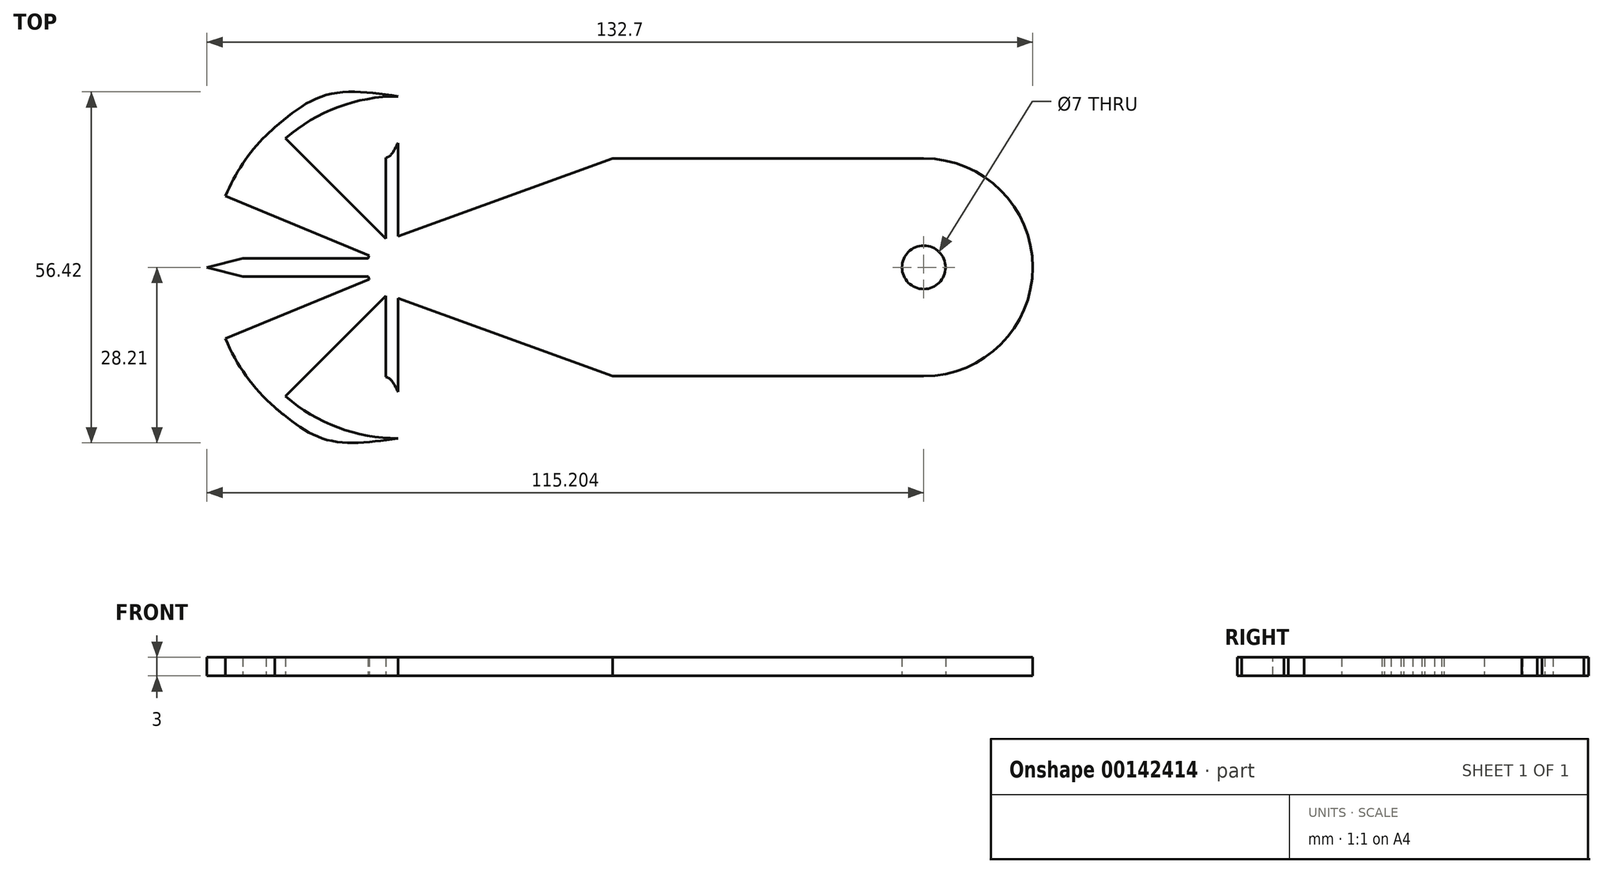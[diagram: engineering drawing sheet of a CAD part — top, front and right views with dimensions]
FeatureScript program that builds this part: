
annotation { "Feature Type Name" : "Feature", "Feature Type Description" : "" }
export const myFeature = defineFeature(function(context is Context, id is Id, definition is map)
    precondition{}
    {
        {
            var Q0;
            Q0=qCreatedBy(makeId("Top.planeOp"),FACE);
            var sketch = newSketch(context, id + "F0", { "sketchPlane" : qUnion([Q0])});
            skLineSegment(sketch, "E0", {"start": v(-142.5, 0) * mm, "end": v(-112.5, 0) * mm, "construction": true});
            skPoint(sketch, "E0.endSnap0", {"position": v(-142.5, 0) * mm});
            skArc(sketch, "E1", {"start": v(-117.12, 1.91) * mm, "mid": v(-117.2, 1.7) * mm, "end": v(-117.28, 1.46) * mm});
            skLineSegment(sketch, "E2", {"start": v(-112.5, 5) * mm, "end": v(-112.5, -5) * mm, "construction": true});
            skLineSegment(sketch, "E3", {"start": v(-112.5, 0) * mm, "end": v(-107.5, 0) * mm, "construction": true});
            skLineSegment(sketch, "E4", {"start": v(-112.5, 0) * mm, "end": v(-117.5, 0) * mm, "construction": true});
            skLineSegment(sketch, "E5", {"start": v(-117.5, 0) * mm, "end": v(-112.5, 5) * mm, "construction": true});
            skLineSegment(sketch, "E6", {"start": v(-112.5, 0) * mm, "end": v(-115, 2.5) * mm, "construction": true});
            skLineSegment(sketch, "E7", {"start": v(-112.5, 5) * mm, "end": v(-107.5, 0) * mm, "construction": true});
            skLineSegment(sketch, "E8", {"start": v(-107.5, 0) * mm, "end": v(-112.5, -5) * mm, "construction": true});
            skLineSegment(sketch, "E9", {"start": v(-112.5, -5) * mm, "end": v(-117.5, 0) * mm, "construction": true});
            skLineSegment(sketch, "E10", {"start": v(-115, 2.5) * mm, "end": v(-116.04, 3.54) * mm, "construction": true});
            skLineSegment(sketch, "E11", {"start": v(-112.5, 0) * mm, "end": v(-115, -2.5) * mm, "construction": true});
            skLineSegment(sketch, "E12", {"start": v(-115, -2.5) * mm, "end": v(-116.04, -3.54) * mm, "construction": true});
            skLineSegment(sketch, "E13", {"start": v(-116.04, 3.54) * mm, "end": v(-116.04, -3.54) * mm, "construction": true});
            skLineSegment(sketch, "E14", {"start": v(-116.04, 3.54) * mm, "end": v(-108.96, 3.54) * mm, "construction": true});
            skLineSegment(sketch, "E15", {"start": v(-108.96, 3.54) * mm, "end": v(-108.96, -3.54) * mm, "construction": true});
            skLineSegment(sketch, "E16", {"start": v(-108.96, -3.54) * mm, "end": v(-116.04, -3.54) * mm, "construction": true});
            skLineSegment(sketch, "E17", {"start": v(-116.04, 1.46) * mm, "end": v(-117.28, 1.46) * mm, "construction": true});
            skLineSegment(sketch, "E18", {"start": v(-116.04, -1.46) * mm, "end": v(-117.28, -1.46) * mm, "construction": true});
            skLineSegment(sketch, "E19", {"start": v(-117.28, 1.46) * mm, "end": v(-135.56, 1.46) * mm});
            skLineSegment(sketch, "E20", {"start": v(-117.28, -1.46) * mm, "end": v(-135.56, -1.46) * mm});
            skLineSegment(sketch, "E21", {"start": v(-112.5, 0) * mm, "end": v(-116.04, -1.46) * mm, "construction": true});
            skLineSegment(sketch, "E22", {"start": v(-116.04, -1.46) * mm, "end": v(-117.12, -1.91) * mm, "construction": true});
            skLineSegment(sketch, "E23", {"start": v(-112.5, 0) * mm, "end": v(-116.04, 1.46) * mm, "construction": true});
            skLineSegment(sketch, "E24", {"start": v(-116.04, 1.46) * mm, "end": v(-117.12, 1.91) * mm, "construction": true});
            skLineSegment(sketch, "E25", {"start": v(-112.5, 0) * mm, "end": v(-113.96, -3.54) * mm, "construction": true});
            skLineSegment(sketch, "E26", {"start": v(-113.96, -3.54) * mm, "end": v(-114.41, -4.62) * mm, "construction": true});
            skLineSegment(sketch, "E27", {"start": v(-112.5, 0) * mm, "end": v(-113.96, 3.54) * mm, "construction": true});
            skLineSegment(sketch, "E28", {"start": v(-113.96, 3.54) * mm, "end": v(-114.41, 4.62) * mm, "construction": true});
            skLineSegment(sketch, "E29", {"start": v(-114.41, -4.62) * mm, "end": v(-127.3, -17.5) * mm});
            skLineSegment(sketch, "E30", {"start": v(-127.3, -17.5) * mm, "end": v(-130.55, -20.75) * mm});
            skArc(sketch, "E31.trimOffspring", {"start": v(-133.71, -21.21) * mm, "mid": v(-133.03, -21.88) * mm, "end": v(-132.32, -22.52) * mm, "construction": true});
            skArc(sketch, "E32.trimOffspring", {"start": v(-133.71, -21.21) * mm, "mid": v(-133.03, -21.88) * mm, "end": v(-132.32, -22.52) * mm});
            skLineSegment(sketch, "E33", {"start": v(-142.5, 0) * mm, "end": v(-143.2, 0) * mm, "construction": true});
            skLineSegment(sketch, "E34", {"start": v(-137.46, 1.46) * mm, "end": v(-143.2, 0) * mm});
            skLineSegment(sketch, "E35", {"start": v(-143.2, 0) * mm, "end": v(-137.46, -1.46) * mm});
            skLineSegment(sketch, "E36.trimOffspring", {"start": v(-142.46, -1.46) * mm, "end": v(-142.5, -1.46) * mm});
            skLineSegment(sketch, "E37.trimOffspring", {"start": v(-142.46, 1.46) * mm, "end": v(-142.5, 1.46) * mm});
            skLineSegment(sketch, "E38", {"start": v(-112.5, 0) * mm, "end": v(-143.2, 0) * mm, "construction": true});
            skArc(sketch, "E39", {"start": v(-143.2, 0) * mm, "mid": v(-127.88, 26.57) * mm, "end": v(-97.2, 26.62) * mm, "construction": true});
            skArc(sketch, "E40", {"start": v(-143.2, 0) * mm, "mid": v(-130.41, -24.93) * mm, "end": v(-102.7, -29.1) * mm, "construction": true});
            skArc(sketch, "E41", {"start": v(-132.32, -22.52) * mm, "mid": v(-131.6, -23.14) * mm, "end": v(-130.86, -23.73) * mm});
            skLineSegment(sketch, "E42", {"start": v(-112.5, 0) * mm, "end": v(-112.5, -30) * mm, "construction": true});
            skLineSegment(sketch, "E43", {"start": v(-112.5, 0) * mm, "end": v(-112.5, 5) * mm, "construction": true});
            skLineSegment(sketch, "E44", {"start": v(-112.5, 0) * mm, "end": v(-116.04, -3.54) * mm, "construction": true});
            skArc(sketch, "E45", {"start": v(-133.71, -21.21) * mm, "mid": v(-132.32, -22.52) * mm, "end": v(-130.86, -23.73) * mm});
            skArc(sketch, "E46", {"start": v(-130.55, -20.75) * mm, "mid": v(-122.13, -25.76) * mm, "end": v(-112.5, -27.5) * mm});
            skFitSpline(sketch, "E47", {"points": [v(-132.32, -22.52) * mm, v(-123.98, -27.72) * mm, v(-112.5, -27.5) * mm], "startDerivative": vector(16.2, -13.5) * mm, "endDerivative": vector(23.33, 3.33) * mm});
            skLineSegment(sketch, "E48", {"start": v(-78, 17.5) * mm, "end": v(-112.5, 5) * mm});
            skLineSegment(sketch, "E49.MirrorCS", {"start": v(-117.12, -1.91) * mm, "end": v(-136.58, -9.98) * mm, "construction": true});
            skLineSegment(sketch, "E50.trimOffspring", {"start": v(-137.42, -1.46) * mm, "end": v(-137.46, -1.46) * mm});
            skLineSegment(sketch, "E51.trimOffspring", {"start": v(-137.42, 1.46) * mm, "end": v(-137.46, 1.46) * mm});
            skPoint(sketch, "E52.orphan", {"position": v(-137.46, 0) * mm});
            skArc(sketch, "E53.trimOffspring", {"start": v(-117.28, -1.46) * mm, "mid": v(-117.2, -1.7) * mm, "end": v(-117.12, -1.91) * mm});
            skLineSegment(sketch, "E54.trimOffspring", {"start": v(-114.41, -4.62) * mm, "end": v(-114.41, -4.62) * mm});
            skArc(sketch, "E55", {"start": v(-133.71, -21.21) * mm, "mid": v(-137.44, -16.67) * mm, "end": v(-140.22, -11.48) * mm});
            skLineSegment(sketch, "E56", {"start": v(-117.12, -1.91) * mm, "end": v(-140.22, -11.48) * mm});
            skPoint(sketch, "E57.trimOffspring.end.orphan", {"position": v(-131.95, -19.45) * mm});
            skPoint(sketch, "E58.start.orphan", {"position": v(-130.18, -17.68) * mm});
            skLineSegment(sketch, "E59", {"start": v(-135.56, 1.46) * mm, "end": v(-137.42, 1.46) * mm});
            skLineSegment(sketch, "E60", {"start": v(-135.56, -1.46) * mm, "end": v(-137.42, -1.46) * mm});
            skLineSegment(sketch, "E61", {"start": v(-112.5, -5) * mm, "end": v(-112.5, -20) * mm});
            skLineSegment(sketch, "E62", {"start": v(-114.41, -4.62) * mm, "end": v(-114.41, -17.62) * mm});
            skLineSegment(sketch, "E63", {"start": v(-114.41, 4.62) * mm, "end": v(-114.41, 17.62) * mm});
            skLineSegment(sketch, "E64.trimOffspring", {"start": v(-112.5, 15.35) * mm, "end": v(-112.5, 30.7) * mm, "construction": true});
            skLineSegment(sketch, "E65", {"start": v(-112.5, 5) * mm, "end": v(-112.5, 20) * mm});
            skFitSpline(sketch, "E66", {"points": [v(-114.41, 17.62) * mm, v(-113.69, 18.03) * mm, v(-112.5, 20) * mm], "startDerivative": vector(1.95, 0.7) * mm, "endDerivative": vector(1.89, 3.81) * mm});
            skFitSpline(sketch, "E67.MirrorCS", {"points": [v(-114.41, -17.62) * mm, v(-113.69, -18.03) * mm, v(-112.5, -20) * mm], "startDerivative": vector(1.95, -0.7) * mm, "endDerivative": vector(1.89, -3.81) * mm});
            skLineSegment(sketch, "E68", {"start": v(0, 0) * mm, "end": v(-160.81, 0) * mm, "construction": true});
            skLineSegment(sketch, "E69.MirrorCS", {"start": v(-78, -17.5) * mm, "end": v(-112.5, -5) * mm});
            skLineSegment(sketch, "E70", {"start": v(-78, 17.5) * mm, "end": v(-28, 17.5) * mm});
            skLineSegment(sketch, "E71", {"start": v(-78, -17.5) * mm, "end": v(-28, -17.5) * mm});
            skLineSegment(sketch, "E72", {"start": v(-28, -17.5) * mm, "end": v(-28, 17.5) * mm, "construction": true});
            skArc(sketch, "E73", {"start": v(-28, -17.5) * mm, "mid": v(-10.5, 0) * mm, "end": v(-28, 17.5) * mm});
            skCircle(sketch, "E74", {"center": v(-28, 0) * mm, "radius": 3.5 * mm});
            skLineSegment(sketch, "E75.MirrorCS", {"start": v(-117.12, 1.91) * mm, "end": v(-136.58, 9.98) * mm, "construction": true});
            skLineSegment(sketch, "E76.MirrorCS", {"start": v(-117.12, 1.91) * mm, "end": v(-140.22, 11.48) * mm});
            skLineSegment(sketch, "E77.MirrorCS", {"start": v(-114.41, 4.62) * mm, "end": v(-127.3, 17.5) * mm});
            skLineSegment(sketch, "E78.MirrorCS", {"start": v(-127.3, 17.5) * mm, "end": v(-130.55, 20.75) * mm});
            skArc(sketch, "E79.MirrorCS", {"start": v(-130.55, 20.75) * mm, "mid": v(-122.13, 25.76) * mm, "end": v(-112.5, 27.5) * mm});
            skFitSpline(sketch, "E80.MirrorCS", {"points": [v(-132.32, 22.52) * mm, v(-123.98, 27.72) * mm, v(-112.5, 27.5) * mm], "startDerivative": vector(16.2, 13.5) * mm, "endDerivative": vector(23.33, -3.33) * mm});
            skArc(sketch, "E81.MirrorCS", {"start": v(-133.71, 21.21) * mm, "mid": v(-137.44, 16.67) * mm, "end": v(-140.22, 11.48) * mm});
            skArc(sketch, "E82.MirrorCS", {"start": v(-133.71, 21.21) * mm, "mid": v(-133.03, 21.88) * mm, "end": v(-132.32, 22.52) * mm, "construction": true});
            skLineSegment(sketch, "E83", {"start": v(-133.71, 21.21) * mm, "end": v(-132.32, 22.52) * mm});
            skSolve(sketch);
        }
        {
            var Q0;
            Q0=makeQuery(id+"F0.imprint","IMPRINT",FACE,{"disambiguationData":[TD([[makeQuery(id+"F0.imprint","IMPRINT",EDGE,{"derivedFrom":sQuery(id+"F0.wireOp",EDGE,"ziCk4KGp-JqVB-bp3Z-GpHH-EpbCwWe1Egps")}),1.0]])]});
            var Q1;
            {var subQ1=sQuery(id+"F0.wireOp",EDGE,"uhgcn0MA-lmyk-5xuW-CFDd-lou4gFRCYRbz");Q1=makeQuery(id+"F0.imprint","IMPRINT",FACE,{"disambiguationData":[TD([[makeQuery(id+"F0.imprint","IMPRINT",EDGE,{"derivedFrom":subQ1}),-1.0]])]});}
            var Q2;
            {var subQ1=sQuery(id+"F0.wireOp",EDGE,"fhOqzcse-Oa16-kai1-nyoO-UOFY2piaUjyF");Q2=makeQuery(id+"F0.imprint","IMPRINT",FACE,{"disambiguationData":[TD([[makeQuery(id+"F0.imprint","IMPRINT",EDGE,{"derivedFrom":subQ1}),-1.0]])]});}
            var Q3;
            {var subQ2=sQuery(id+"F0.wireOp",EDGE,"E19");Q3=makeQuery(id+"F0.imprint","IMPRINT",FACE,{"disambiguationData":[TD([[makeQuery(id+"F0.imprint","IMPRINT",EDGE,{"derivedFrom":subQ2}),1.0]])]});}
            var Q4;
            {var subQ1=sQuery(id+"F0.wireOp",EDGE,"Veo52X2X-XMnk-9I4A-QR4Y-ZCmek0ntMTCH");Q4=makeQuery(id+"F0.imprint","IMPRINT",FACE,{"disambiguationData":[TD([[makeQuery(id+"F0.imprint","IMPRINT",EDGE,{"derivedFrom":subQ1}),1.0]])]});}
            var Q5;
            {var subQ0=sQuery(id+"F0.wireOp",EDGE,"K1bhA7Ta-bAuJ-rcCs-RFPl-E3xBNxquXvMg");Q5=makeQuery(id+"F0.imprint","IMPRINT",FACE,{"disambiguationData":[TD([[makeQuery(id+"F0.imprint","IMPRINT",EDGE,{"derivedFrom":subQ0}),1.0]])]});}
            var Q6;
            {var subQ0=sQuery(id+"F0.wireOp",EDGE,"E1");var subQ6=makeQuery(id+"F0.imprint","INTERSECT",VERTEX,{"derivedFrom":[subQ0,sQuery(id+"F0.wireOp",EDGE,"aQuUePQg-7TdR-qp2c-H8yb-7XBCCwPh9dnY")]});Q6=makeQuery(id+"F0.imprint","IMPRINT",FACE,{"disambiguationData":[TD([[makeQuery(id+"F0.imprint","IMPRINT",EDGE,{"disambiguationData":[TD([[subQ6,1.0]])],"derivedFrom":subQ0}),1.0]])]});}
            extrude(context, id + "F1", {"entities" : qUnion([Q0, Q1, Q2, Q3, Q4, Q5, Q6]), "endBound" : BoundingType.SYMMETRIC, "depth" : 3 * mm});
        }
    });
